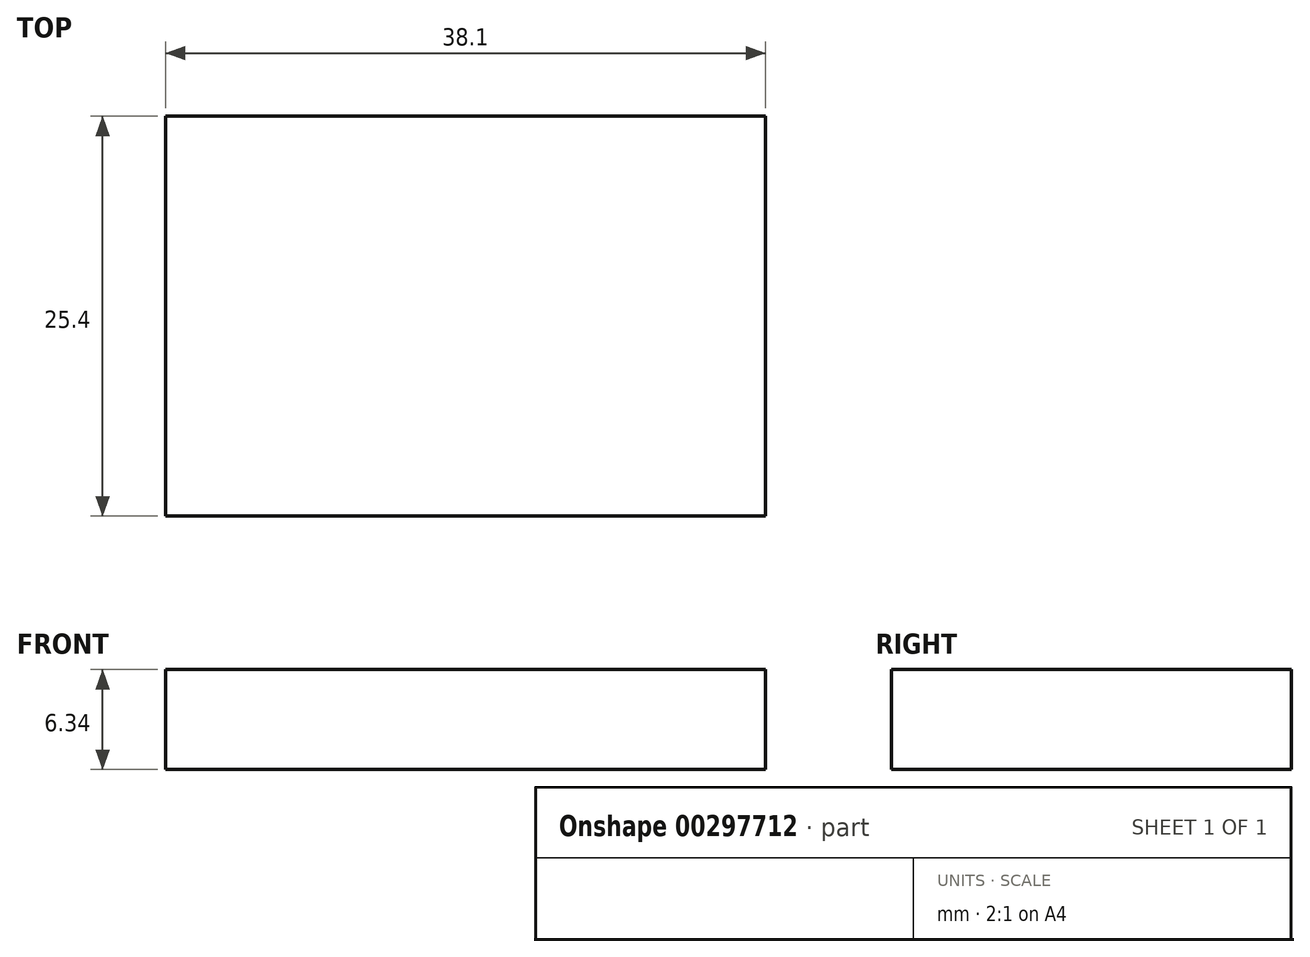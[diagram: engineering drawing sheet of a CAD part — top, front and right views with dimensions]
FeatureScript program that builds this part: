
annotation { "Feature Type Name" : "Feature", "Feature Type Description" : "" }
export const myFeature = defineFeature(function(context is Context, id is Id, definition is map)
    precondition{}
    {
        {
            var Q0;
            Q0=qCreatedBy(makeId("Front.planeOp"),FACE);
            var sketch = newSketch(context, id + "F0", { "sketchPlane" : qUnion([Q0])});
            skLineSegment(sketch, "E0.bottom", {"start": v(-19.05, -3.18) * mm, "end": v(19.05, -3.18) * mm});
            skLineSegment(sketch, "E0.top", {"start": v(-19.05, 3.18) * mm, "end": v(19.05, 3.18) * mm});
            skLineSegment(sketch, "E0.left", {"start": v(-19.05, -3.17) * mm, "end": v(-19.05, 3.18) * mm});
            skLineSegment(sketch, "E0.right", {"start": v(19.05, -3.18) * mm, "end": v(19.05, 3.17) * mm});
            skPoint(sketch, "E0.middle", {"position": v(0, 0) * mm});
            skSolve(sketch);
        }
        {
            var Q0;
            Q0 = qSketchRegion(id + "F0", true);
            extrude(context, id + "F1", {"entities" : qUnion([Q0]), "depth" : 25.4 * mm});
        }
    });
